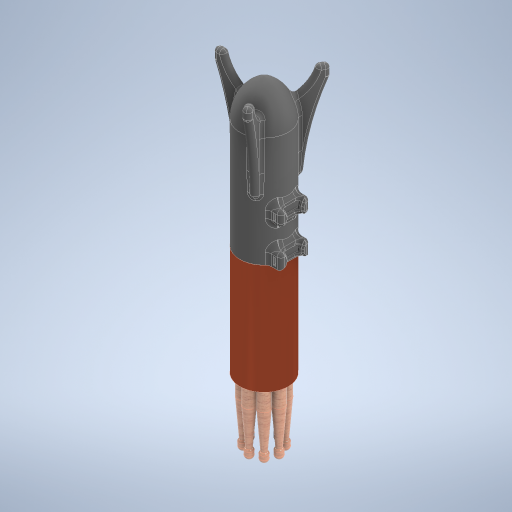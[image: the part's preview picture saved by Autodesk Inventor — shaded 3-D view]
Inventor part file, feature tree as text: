
AUTODESK INVENTOR PART (.ipt)
format: ipt  version: 2023 (Build 270158030, 158C)  size: 1,767,936 bytes
history: native  units: mm
features: fillet x17, sketch x15, extrude x14, other x12, plane x4, revolve x3, pattern_circular x2, pattern_linear x1, mirror x1, chamfer x1
ambient origin geometry x8: Origin, YZ Plane, XZ Plane, XY Plane, X Axis, Y Axis, Z Axis, Center Point
bodies: Body1 (feature_tree), Body2 (feature_tree), Body3 (feature_tree), Body4 (feature_tree), Body5 (feature_tree), Body6 (feature_tree), Body7 (feature_tree)
feature tree (70):
  other  "stage-one"
  extrude  "body-tube"  Depth=3.0mm
  extrude  "Extrusion2"  Depth=20.0mm
  extrude  "Extrusion3"  Depth=10.0mm
  plane  "Work Plane2"
  plane  "Work Plane4"
  extrude  "Extrusion4"  Depth=12.5mm
  plane  "Work Plane6"
  pattern_linear  "Rectangular Pattern1"  Count1=2  [1 undecoded]
  extrude  "Extrusion7"  Depth=6.0mm
  other  "Work Point2"
  revolve  "Revolution2"  [1 undecoded]
  mirror  "Mirror1"
  extrude  "Extrusion5"  Depth=4.0mm
  fillet  "Fillet1"  [1 undecoded]
  fillet  "Fillet2"  Radius=30.0mm
  fillet  "Fillet3"  Radius=200.0mm
  chamfer  "Chamfer1"  Distance=20.0mm
  fillet  "Fillet4"  Radius=7.0mm
  fillet  "Fillet5"  Radius=7.0mm
  fillet  "Fillet6"  Radius=5.0mm
  extrude  "Extrusion6"  Depth=2.0mm TaperAngle=45.0deg
  extrude  "Extrusion8"  Depth=5.0mm
  pattern_circular  "Circular Pattern1"  [2 undecoded]
  fillet  "Fillet7"  Radius=8.0mm
  fillet  "Fillet9"  Radius=10.0mm
  fillet  "Fillet10"  Radius=3.5mm
  fillet  "Fillet11"  [1 undecoded]
  fillet  "Fillet12"  Radius=1.0mm
  fillet  "Fillet13"  Radius=50.0mm
  extrude  "Extrusion9"  Depth=200.0mm
  extrude  "Extrusion10"  TaperAngle=90.0deg  [1 undecoded]
  extrude  "Extrusion11"  Depth=48.0mm
  extrude  "Extrusion12"  Depth=5.0mm
  other  "Work Point3"
  fillet  "Fillet15"  Radius=65.0mm
  fillet  "Fillet16"  Radius=15.0mm
  plane  "Work Plane7"
  extrude  "Extrusion14"  Depth=5.0mm
  revolve  "Revolution4"  [1 undecoded]
  fillet  "Fillet18"  Radius=126.0mm
  fillet  "Fillet19"  Radius=404.0mm
  fillet  "Fillet20"  Radius=150.0mm
  pattern_circular  "Circular Pattern2"  [2 undecoded]
  revolve  "Revolution3"  [1 undecoded]
  extrude  "Extrusion13"  Depth=5.0mm
  sketch  "Sketch1"  dims[d0=60.0mm d1=3.0mm]
  other  "rail-clamp-A"
  sketch  "Sketch5"  dims[d2=150.0mm d3=0.0mm d19=20.0mm]
  sketch  "Sketch6"  dims[d20=20.0mm d22=10.0mm]
  other  "Holding Bar"
  sketch  "Sketch8"  dims[d23=20.0mm d24=0.0mm d26=12.5mm]
  other  "bar-vertical"
  other  "Pattern of Holding Bar:1"
  other  "bar-angled"
  sketch  "Sketch9"  dims[d27=12.5mm]
  sketch  "Sketch10"  dims[d28=15.0mm]
  sketch  "Sketch11"  dims[d29=17.0mm]
  sketch  "Sketch12"  dims[d30=17.0mm]
  sketch  "Sketch13"  dims[d31=3.490659mm]
  sketch  "Sketch14"  dims[d33=3.490659mm]
  other  "stage-two"
  sketch  "Sketch15"  dims[d34=53.0mm d35=20.0mm]
  sketch  "Sketch16"  dims[d36=6.0mm d37=6.0mm]
  sketch  "Sketch17"  dims[d38=7.5mm d39=0.0mm d40=30.0mm]
  other  "nose-cone"
  sketch  "Sketch19"  dims[d41=53.296162mm d42=4.0mm]
  other  "drumsticks"
  sketch  "Sketch20"  dims[d43=200.0mm d44=100.0mm d45=0.0mm d46=0.0mm d47=90.0deg d49=30.0mm d50=200.0mm d51=100.0mm d52=0.0mm d53=0.0mm d56=20.0mm d58=50.0mm d59=7.0mm d60=7.0mm d61=5.0mm d62=2.0mm d63=2.0mm d64=45.0deg d65=5.0mm d66=5.0mm d67=8.0mm d68=10.0mm d70=3.5mm d76=0.0mm d77=0.0mm d78=1.0mm d79=50.0mm d80=0.0mm d85=53.0mm d86=52.992097mm d88=3.0mm d89=3.0mm d90=54.0mm d91=200.0mm d92=90.0deg d93=48.0mm d94=5.0mm d95=65.0mm d96=15.0mm d97=5.0mm d98=367.0mm d99=126.0mm d100=404.0mm d101=150.0mm d102=10.0mm d103=0.0mm d104=5.0mm d106=5.0mm d107=30.0mm d108=360.0deg d110=5.0mm d111=5.0mm d112=5.0mm d113=5.0mm d115=3.0mm d116=1.5mm d117=50.0mm d118=0.0mm d119=150.0mm d120=0.0mm d121=1.5mm d122=49.0mm d123=0.0mm d124=1.5mm d125=30.0mm d126=0.0mm d131=360.0deg d132=1.5mm d133=29.0mm d134=0.0mm d135=3.0mm d136=2.5mm d137=10.0mm d138=2.0mm d139=1.5mm d140=-110.0mm d141=15.0mm d142=400.0mm d143=0.0mm d144=15.0mm d145=0.0mm d147=19.0mm d148=15.0mm d149=410.0mm d150=7.5mm d151=13.0mm d152=10.5mm d153=2.25mm d154=2.25mm d159=3.85mm d160=3.85mm d161=50.0mm d162=2.0mm d163=50.0mm d164=339.5mm d165=360.0deg d166=5.0mm d167=3.0mm d168=10.0mm d169=80.0mm d170=360.0deg d180=3.0mm d181=3.0mm]
  other  "stick"
note: 11 required parameter values undecoded (feature->parameter linkage not recoverable at this tier; creation-order binding heuristic only, values carry confidence <= 0.55)